# Revit family: Batidora_B-20_GENERADO
name_source: partatom
category: Equipos especializados
revit_build: Autodesk Revit 2014 (Build: 20131024_2115(x64)
units: mm (PartAtom-declared; Revit-internal decimal feet)

## types (6) — shared parameters
Cycle = 50 Hz
Fabricante = SAMMIC S.L.
Foodservice Equipment Identifier = Sí
Phase = 1
Revision Code = 1
URL = https://www.sammic.com

## per-type parameters (varying)
| type | Comentarios de tipo | FL Amps | Modelo | Specification by Manufacturer | URL Cutsheet | Volts | Weight in Pounds |
| Immersion blender & whisk combo MB-21 230/50-60/1 | Professional hand blender and beater. 300 W. | 1 A | 3030634 | Variable speed motor block.
250 mm detachable mixer arm designed for continuous use in recipients of up to 12 litres.
Whisk with capacity for 2 to 30 egg whites. | http://www.sammic.com | 230 V | 7.8 |
| Immersion blender & whisk combo MB-21 230/50-60/1 UK | Professional hand blender and beater. 300 W. | 1 A | 3030760 | Variable speed motor block.
250 mm detachable mixer arm designed for continuous use in recipients of up to 12 litres.
Whisk with capacity for 2 to 30 egg whites. | http://www.sammic.com | 230 V | 7.8 |
| Immersion blender & whisk combo MB-21 120/50-60/1 USA | Professional hand blender and beater. 300 W. | 2 A | 3030764 | Variable speed motor block.
250 mm detachable mixer arm designed for continuous use in recipients of up to 12 litres.
Whisk with capacity for 2 to 30 egg whites. | http://www.sammic.com | 120 V | 7.8 |
| Immersion blender & whisk combo MB-21 230/50-60/1 AUS | Professional hand blender and beater. 300 W. | 1 A | 3030762 | Variable speed motor block.
250 mm detachable mixer arm designed for continuous use in recipients of up to 12 litres.
Whisk with capacity for 2 to 30 egg whites. | http://www.sammic.com | 230 V | 7.8 |
| Immersion blender & whisk combo MB-21 120/50-60/1 MX | Professional hand blender and beater. 300 W. | 0 A | 3030765 | Variable speed motor block.
250 mm detachable mixer arm designed for continuous use in recipients of up to 12 litres.
Whisk with capacity for 2 to 30 egg whites. |  | 0 V | 7.8 |
| Beater B-20 230/50-60/1 | Professional beater. 300 W. | 1 A | 3030766 | Variable speed motor block.
Whisk with capacity for 2 to 30 egg whites. | http://www.sammic.com | 230 V | 5.8 |

note: column(s) folded — value = type name in every type: Descripción
